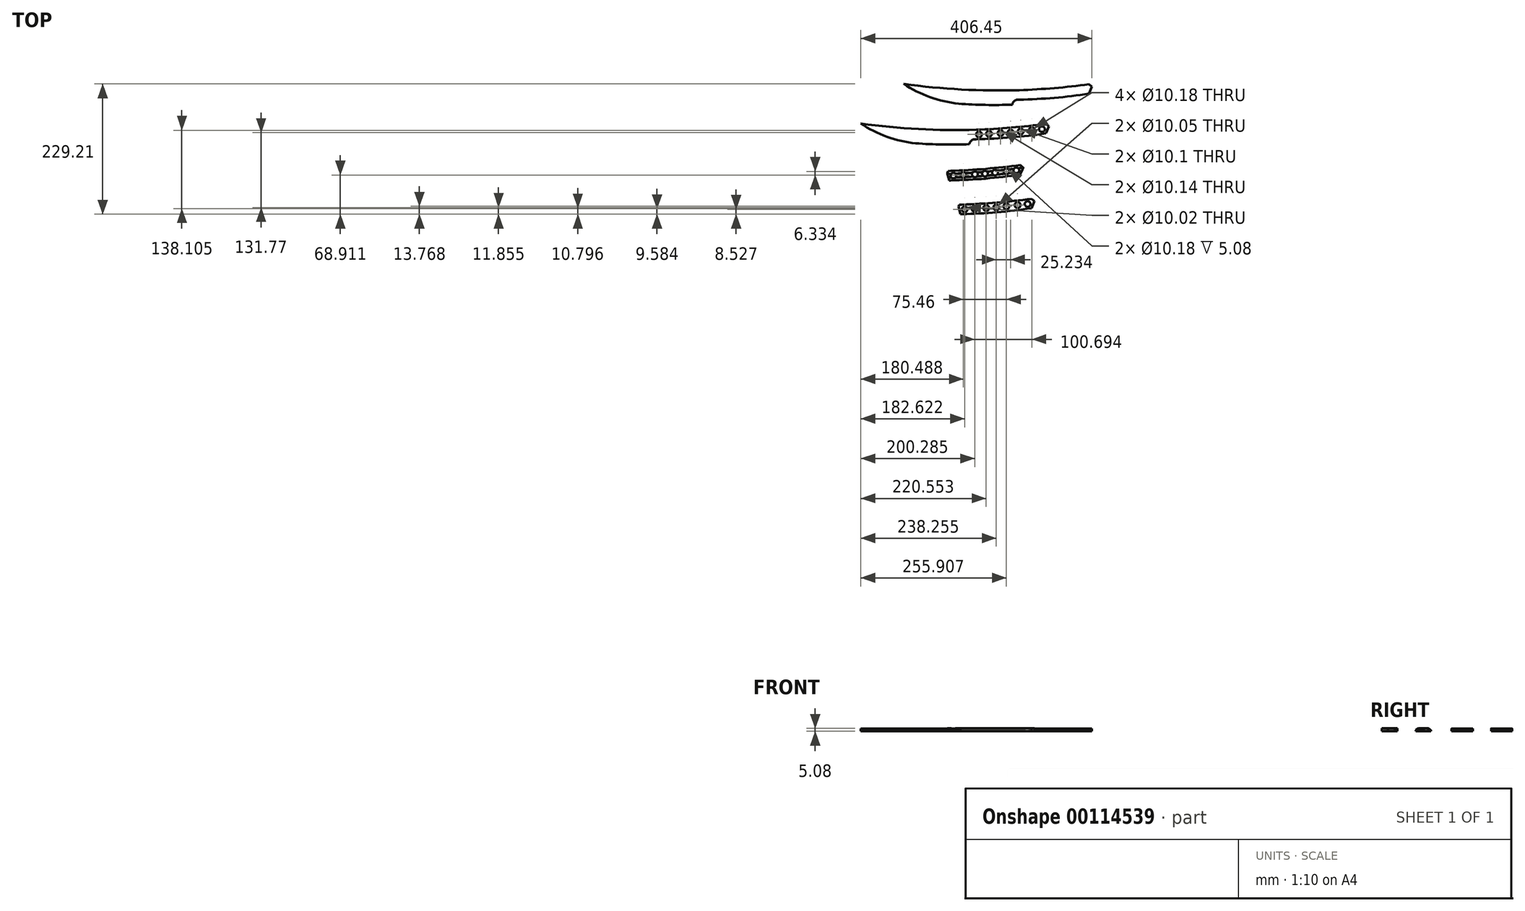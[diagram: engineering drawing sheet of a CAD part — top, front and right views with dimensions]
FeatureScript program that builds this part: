
annotation { "Feature Type Name" : "Feature", "Feature Type Description" : "" }
export const myFeature = defineFeature(function(context is Context, id is Id, definition is map)
    precondition{}
    {
        {
            var Q0;
            Q0=qCreatedBy(makeId("Top.planeOp"),FACE);
            var sketch = newSketch(context, id + "F0", { "sketchPlane" : qUnion([Q0])});
            skArc(sketch, "E0", {"start": v(-65.3, 17.64) * mm, "mid": v(-4.03, 20.86) * mm, "end": v(56.9, 28.1) * mm});
            skArc(sketch, "E1", {"start": v(-65.3, 34.32) * mm, "mid": v(-4.08, 38.03) * mm, "end": v(56.9, 44.62) * mm});
            skLineSegment(sketch, "E2", {"start": v(56.9, 28.1) * mm, "end": v(62.29, 40.27) * mm});
            skLineSegment(sketch, "E3", {"start": v(62.29, 40.27) * mm, "end": v(56.9, 44.62) * mm});
            skArc(sketch, "E4", {"start": v(-268.6, 45.37) * mm, "mid": v(-167.18, 35.59) * mm, "end": v(-65.3, 34.32) * mm});
            skArc(sketch, "E5", {"start": v(-172.08, 10.53) * mm, "mid": v(-124.86, 8.37) * mm, "end": v(-77.6, 8.91) * mm});
            skArc(sketch, "E6", {"start": v(-268.6, 45.37) * mm, "mid": v(-222.44, 22.12) * mm, "end": v(-172.08, 10.53) * mm});
            skLineSegment(sketch, "E7", {"start": v(-65.3, 17.64) * mm, "end": v(-68.39, 17.58) * mm});
            skArc(sketch, "E8", {"start": v(-68.39, 17.58) * mm, "mid": v(-74.66, 15.02) * mm, "end": v(-77.6, 8.91) * mm});
            skSolve(sketch);
        }
        {
            var Q0;
            Q0=makeQuery(id+"F0.imprint","IMPRINT",FACE,{"disambiguationData":[TD([[makeQuery(id+"F0.imprint","IMPRINT",EDGE,{"derivedFrom":sQuery(id+"F0.wireOp",EDGE,"E0")}),1.0]])]});
            extrude(context, id + "F1", {"entities" : qUnion([Q0]), "depth" : 4.75 * mm});
        }
        {
            var Q0;
            Q0=qCreatedBy(makeId("Top.planeOp"),FACE);
            var sketch = newSketch(context, id + "F2", { "sketchPlane" : qUnion([Q0])});
            skArc(sketch, "E9", {"start": v(-140.87, -52.01) * mm, "mid": v(-79.6, -48.8) * mm, "end": v(-18.66, -41.55) * mm});
            skArc(sketch, "E10", {"start": v(-140.87, -35.34) * mm, "mid": v(-79.65, -31.63) * mm, "end": v(-18.66, -25.03) * mm});
            skLineSegment(sketch, "E11", {"start": v(-18.66, -41.55) * mm, "end": v(-13.28, -29.4) * mm});
            skLineSegment(sketch, "E12", {"start": v(-13.28, -29.4) * mm, "end": v(-18.66, -25.03) * mm});
            skArc(sketch, "E13", {"start": v(-344.16, -24.28) * mm, "mid": v(-242.75, -34.07) * mm, "end": v(-140.87, -35.34) * mm});
            skArc(sketch, "E14", {"start": v(-247.65, -59.13) * mm, "mid": v(-200.42, -61.28) * mm, "end": v(-153.16, -60.75) * mm});
            skArc(sketch, "E15", {"start": v(-344.16, -24.28) * mm, "mid": v(-298, -47.54) * mm, "end": v(-247.65, -59.13) * mm});
            skLineSegment(sketch, "E16", {"start": v(-140.87, -52.01) * mm, "end": v(-143.96, -52.07) * mm});
            skArc(sketch, "E17", {"start": v(-143.96, -52.07) * mm, "mid": v(-150.23, -54.64) * mm, "end": v(-153.16, -60.75) * mm});
            skLineSegment(sketch, "E18", {"start": v(-143.96, -52.07) * mm, "end": v(-147.1, -38.76) * mm});
            skLineSegment(sketch, "E19", {"start": v(-147.1, -38.76) * mm, "end": v(-145.57, -35.47) * mm});
            skLineSegment(sketch, "E20", {"start": v(-81.75, -30.63) * mm, "end": v(-81.75, -31.63) * mm});
            skCircle(sketch, "E21", {"center": v(-136.3, -43.54) * mm, "radius": 5.01 * mm});
            skCircle(sketch, "E22", {"center": v(-80.67, -40.21) * mm, "radius": 5.03 * mm});
            skCircle(sketch, "E23", {"center": v(-25.56, -34.24) * mm, "radius": 5 * mm});
            skLineSegment(sketch, "E24", {"start": v(-80.67, -40.21) * mm, "end": v(-136.3, -43.54) * mm});
            skLineSegment(sketch, "E25", {"start": v(-80.67, -40.21) * mm, "end": v(-25.56, -34.24) * mm});
            skLineSegment(sketch, "E26", {"start": v(-131.3, -43.24) * mm, "end": v(-116.03, -42.33) * mm});
            skLineSegment(sketch, "E27", {"start": v(-85.69, -40.51) * mm, "end": v(-98.37, -41.27) * mm});
            skLineSegment(sketch, "E28", {"start": v(-131.3, -43.24) * mm, "end": v(-118.64, -42.49) * mm});
            skCircle(sketch, "E29", {"center": v(-98.37, -41.27) * mm, "radius": 5.07 * mm});
            skCircle(sketch, "E30", {"center": v(-118.64, -42.49) * mm, "radius": 5.1 * mm});
            skLineSegment(sketch, "E31", {"start": v(-75.67, -39.67) * mm, "end": v(-63.02, -38.3) * mm});
            skLineSegment(sketch, "E32", {"start": v(-30.53, -34.78) * mm, "end": v(-43.18, -36.15) * mm});
            skCircle(sketch, "E33", {"center": v(-63.02, -38.3) * mm, "radius": 5.05 * mm});
            skCircle(sketch, "E34", {"center": v(-43.18, -36.15) * mm, "radius": 5.09 * mm});
            skSolve(sketch);
        }
        {
            var Q0;
            Q0=makeQuery(id+"F2.imprint","IMPRINT",FACE,{"disambiguationData":[TD([[makeQuery(id+"F2.imprint","IMPRINT",EDGE,{"derivedFrom":sQuery(id+"F2.wireOp",EDGE,"E14")}),1.0]])]});
            var Q1;
            Q1=makeQuery(id+"F2.imprint","IMPRINT",FACE,{"disambiguationData":[TD([[makeQuery(id+"F2.imprint","IMPRINT",EDGE,{"derivedFrom":sQuery(id+"F2.wireOp",EDGE,"E9")}),1.0]])]});
            extrude(context, id + "F3", {"entities" : qUnion([Q0, Q1]), "depth" : 4.75 * mm});
        }
        {
            var Q0;
            Q0=qCreatedBy(makeId("Top.planeOp"),FACE);
            var sketch = newSketch(context, id + "F4", { "sketchPlane" : qUnion([Q0])});
            skArc(sketch, "E35", {"start": v(-166.1, -183.79) * mm, "mid": v(-104.83, -180.57) * mm, "end": v(-43.9, -173.32) * mm});
            skArc(sketch, "E36", {"start": v(-166.1, -167.1) * mm, "mid": v(-104.88, -163.4) * mm, "end": v(-43.9, -156.8) * mm});
            skLineSegment(sketch, "E37", {"start": v(-43.9, -173.32) * mm, "end": v(-38.51, -161.16) * mm});
            skLineSegment(sketch, "E38", {"start": v(-38.51, -161.16) * mm, "end": v(-43.9, -156.8) * mm});
            skLineSegment(sketch, "E39", {"start": v(-166.1, -183.79) * mm, "end": v(-169.19, -183.84) * mm});
            skLineSegment(sketch, "E40", {"start": v(-169.19, -183.84) * mm, "end": v(-172.33, -170.54) * mm});
            skLineSegment(sketch, "E41", {"start": v(-172.33, -170.54) * mm, "end": v(-170.8, -167.24) * mm});
            skLineSegment(sketch, "E42", {"start": v(-106.98, -162.4) * mm, "end": v(-106.98, -163.4) * mm});
            skCircle(sketch, "E43", {"center": v(-161.54, -175.31) * mm, "radius": 5.01 * mm});
            skCircle(sketch, "E44", {"center": v(-105.9, -171.99) * mm, "radius": 5.03 * mm});
            skCircle(sketch, "E45", {"center": v(-50.8, -166.01) * mm, "radius": 5 * mm});
            skLineSegment(sketch, "E46", {"start": v(-105.9, -171.99) * mm, "end": v(-161.54, -175.31) * mm});
            skLineSegment(sketch, "E47", {"start": v(-105.9, -171.99) * mm, "end": v(-50.8, -166.01) * mm});
            skLineSegment(sketch, "E48", {"start": v(-156.54, -175.01) * mm, "end": v(-141.26, -174.1) * mm});
            skLineSegment(sketch, "E49", {"start": v(-110.92, -172.29) * mm, "end": v(-123.6, -173.04) * mm});
            skLineSegment(sketch, "E50", {"start": v(-156.54, -175.01) * mm, "end": v(-143.88, -174.26) * mm});
            skCircle(sketch, "E51", {"center": v(-123.6, -173.04) * mm, "radius": 5.07 * mm});
            skCircle(sketch, "E52", {"center": v(-143.88, -174.26) * mm, "radius": 5.1 * mm});
            skLineSegment(sketch, "E53", {"start": v(-100.9, -171.44) * mm, "end": v(-88.25, -170.07) * mm});
            skLineSegment(sketch, "E54", {"start": v(-55.76, -166.55) * mm, "end": v(-68.42, -167.92) * mm});
            skCircle(sketch, "E55", {"center": v(-88.25, -170.07) * mm, "radius": 5.05 * mm});
            skCircle(sketch, "E56", {"center": v(-68.42, -167.92) * mm, "radius": 5.09 * mm});
            skLineSegment(sketch, "E57", {"start": v(-166.1, -167.1) * mm, "end": v(-170.8, -167.24) * mm});
            skSolve(sketch);
        }
        {
            var Q0;
            Q0=makeQuery(id+"F4.imprint","IMPRINT",FACE,{"disambiguationData":[TD([[makeQuery(id+"F4.imprint","IMPRINT",EDGE,{"derivedFrom":sQuery(id+"F4.wireOp",EDGE,"E35")}),1.0]])]});
            extrude(context, id + "F5", {"entities" : qUnion([Q0]), "depth" : 5.08 * mm});
        }
        {
            var Q0;
            Q0=makeQuery(id+"F5.opExtrude","SWEPT_BODY",BODY,{"disambiguationData":[OSD([sQuery(id+"F4.wireOp",EDGE,"E35"),sQuery(id+"F4.wireOp",EDGE,"E36"),sQuery(id+"F4.wireOp",EDGE,"E37"),sQuery(id+"F4.wireOp",EDGE,"E38"),sQuery(id+"F4.wireOp",EDGE,"E39"),sQuery(id+"F4.wireOp",EDGE,"E40"),sQuery(id+"F4.wireOp",EDGE,"E41"),sQuery(id+"F4.wireOp",EDGE,"E43"),sQuery(id+"F4.wireOp",EDGE,"E44"),sQuery(id+"F4.wireOp",EDGE,"E45"),sQuery(id+"F4.wireOp",EDGE,"E51"),sQuery(id+"F4.wireOp",EDGE,"E52"),sQuery(id+"F4.wireOp",EDGE,"E55"),sQuery(id+"F4.wireOp",EDGE,"E56"),sQuery(id+"F4.wireOp",EDGE,"E57")])]});
            transform(context, id + "F6", {"entities" : qUnion([Q0]), "transformType" : TransformType.TRANSLATION_3D, "dx" : 0 * mm, "dy" : 0 * mm, "dz" : 0 * mm, "makeCopy" : true});
        }
        {
            var Q0;
            Q0=makeQuery(id+"F6.opPattern","COPY",BODY,{"derivedFrom":makeQuery(id+"F5.opExtrude","SWEPT_BODY",BODY,{"disambiguationData":[OSD([sQuery(id+"F4.wireOp",EDGE,"E35"),sQuery(id+"F4.wireOp",EDGE,"E36"),sQuery(id+"F4.wireOp",EDGE,"E37"),sQuery(id+"F4.wireOp",EDGE,"E38"),sQuery(id+"F4.wireOp",EDGE,"E39"),sQuery(id+"F4.wireOp",EDGE,"E40"),sQuery(id+"F4.wireOp",EDGE,"E41"),sQuery(id+"F4.wireOp",EDGE,"E43"),sQuery(id+"F4.wireOp",EDGE,"E44"),sQuery(id+"F4.wireOp",EDGE,"E45"),sQuery(id+"F4.wireOp",EDGE,"E51"),sQuery(id+"F4.wireOp",EDGE,"E52"),sQuery(id+"F4.wireOp",EDGE,"E55"),sQuery(id+"F4.wireOp",EDGE,"E56"),sQuery(id+"F4.wireOp",EDGE,"E57")])]}),"instanceName":"1"});
            deleteBodies(context, id + "F7", {"entities" : qUnion([Q0])});
        }
        {
            var Q0;
            Q0=qCreatedBy(makeId("Top.planeOp"),FACE);
            var sketch = newSketch(context, id + "F8", { "sketchPlane" : qUnion([Q0])});
            skArc(sketch, "E58", {"start": v(-185.9, -124.46) * mm, "mid": v(-124.63, -121.24) * mm, "end": v(-63.7, -114) * mm});
            skArc(sketch, "E59", {"start": v(-185.9, -107.78) * mm, "mid": v(-124.68, -104.07) * mm, "end": v(-63.7, -97.48) * mm});
            skLineSegment(sketch, "E60", {"start": v(-63.7, -114) * mm, "end": v(-58.3, -101.83) * mm});
            skLineSegment(sketch, "E61", {"start": v(-58.3, -101.83) * mm, "end": v(-63.7, -97.48) * mm});
            skLineSegment(sketch, "E62", {"start": v(-185.9, -124.46) * mm, "end": v(-188.99, -124.52) * mm});
            skLineSegment(sketch, "E63", {"start": v(-188.99, -124.52) * mm, "end": v(-192.13, -111.2) * mm});
            skLineSegment(sketch, "E64", {"start": v(-192.13, -111.2) * mm, "end": v(-190.6, -107.91) * mm});
            skLineSegment(sketch, "E65", {"start": v(-126.78, -103.07) * mm, "end": v(-126.78, -104.07) * mm});
            skCircle(sketch, "E66", {"center": v(-181.33, -115.99) * mm, "radius": 5.01 * mm});
            skCircle(sketch, "E67", {"center": v(-125.7, -112.66) * mm, "radius": 5.03 * mm});
            skCircle(sketch, "E68", {"center": v(-70.59, -106.68) * mm, "radius": 5 * mm});
            skLineSegment(sketch, "E69", {"start": v(-125.7, -112.66) * mm, "end": v(-181.33, -115.99) * mm});
            skLineSegment(sketch, "E70", {"start": v(-125.7, -112.66) * mm, "end": v(-70.59, -106.68) * mm});
            skLineSegment(sketch, "E71", {"start": v(-176.33, -115.69) * mm, "end": v(-161.06, -114.77) * mm});
            skLineSegment(sketch, "E72", {"start": v(-130.72, -112.96) * mm, "end": v(-143.4, -113.72) * mm});
            skLineSegment(sketch, "E73", {"start": v(-176.33, -115.69) * mm, "end": v(-163.67, -114.93) * mm});
            skCircle(sketch, "E74", {"center": v(-143.4, -113.72) * mm, "radius": 5.07 * mm});
            skCircle(sketch, "E75", {"center": v(-163.67, -114.93) * mm, "radius": 5.1 * mm});
            skLineSegment(sketch, "E76", {"start": v(-120.7, -112.12) * mm, "end": v(-108.05, -110.74) * mm});
            skLineSegment(sketch, "E77", {"start": v(-75.56, -107.22) * mm, "end": v(-88.21, -108.6) * mm});
            skCircle(sketch, "E78", {"center": v(-108.05, -110.74) * mm, "radius": 5.05 * mm});
            skCircle(sketch, "E79", {"center": v(-88.21, -108.6) * mm, "radius": 5.09 * mm});
            skLineSegment(sketch, "E80", {"start": v(-185.9, -107.78) * mm, "end": v(-190.6, -107.91) * mm});
            skSolve(sketch);
        }
        {
            var Q0;
            Q0=makeQuery(id+"F8.imprint","IMPRINT",FACE,{"disambiguationData":[TD([[makeQuery(id+"F8.imprint","IMPRINT",EDGE,{"derivedFrom":sQuery(id+"F8.wireOp",EDGE,"E58")}),1.0]])]});
            extrude(context, id + "F9", {"entities" : qUnion([Q0]), "depth" : 5.08 * mm});
        }
        {
            var Q0;
            Q0=makeQuery(id+"F9.opExtrude","CAP_EDGE",EDGE,{"disambiguationData":[OSD([sQuery(id+"F8.wireOp",EDGE,"E58")])],"isStart":false});
            chamfer(context, id + "F10", {"entities" : qUnion([Q0]), "chamferType" : ChamferType.TWO_OFFSETS, "width1" : 5.08 * mm, "oppositeDirection" : false, "width2" : 3.05 * mm, "tangentPropagation" : true});
        }
        {
            var Q0;
            Q0=makeQuery(id+"F9.opExtrude","CAP_EDGE",EDGE,{"disambiguationData":[OSD([sQuery(id+"F8.wireOp",EDGE,"E80")])],"isStart":false});
            chamfer(context, id + "F11", {"entities" : qUnion([Q0]), "chamferType" : ChamferType.TWO_OFFSETS, "width1" : 5.08 * mm, "oppositeDirection" : false, "width2" : 3.05 * mm, "tangentPropagation" : true});
        }
    });
